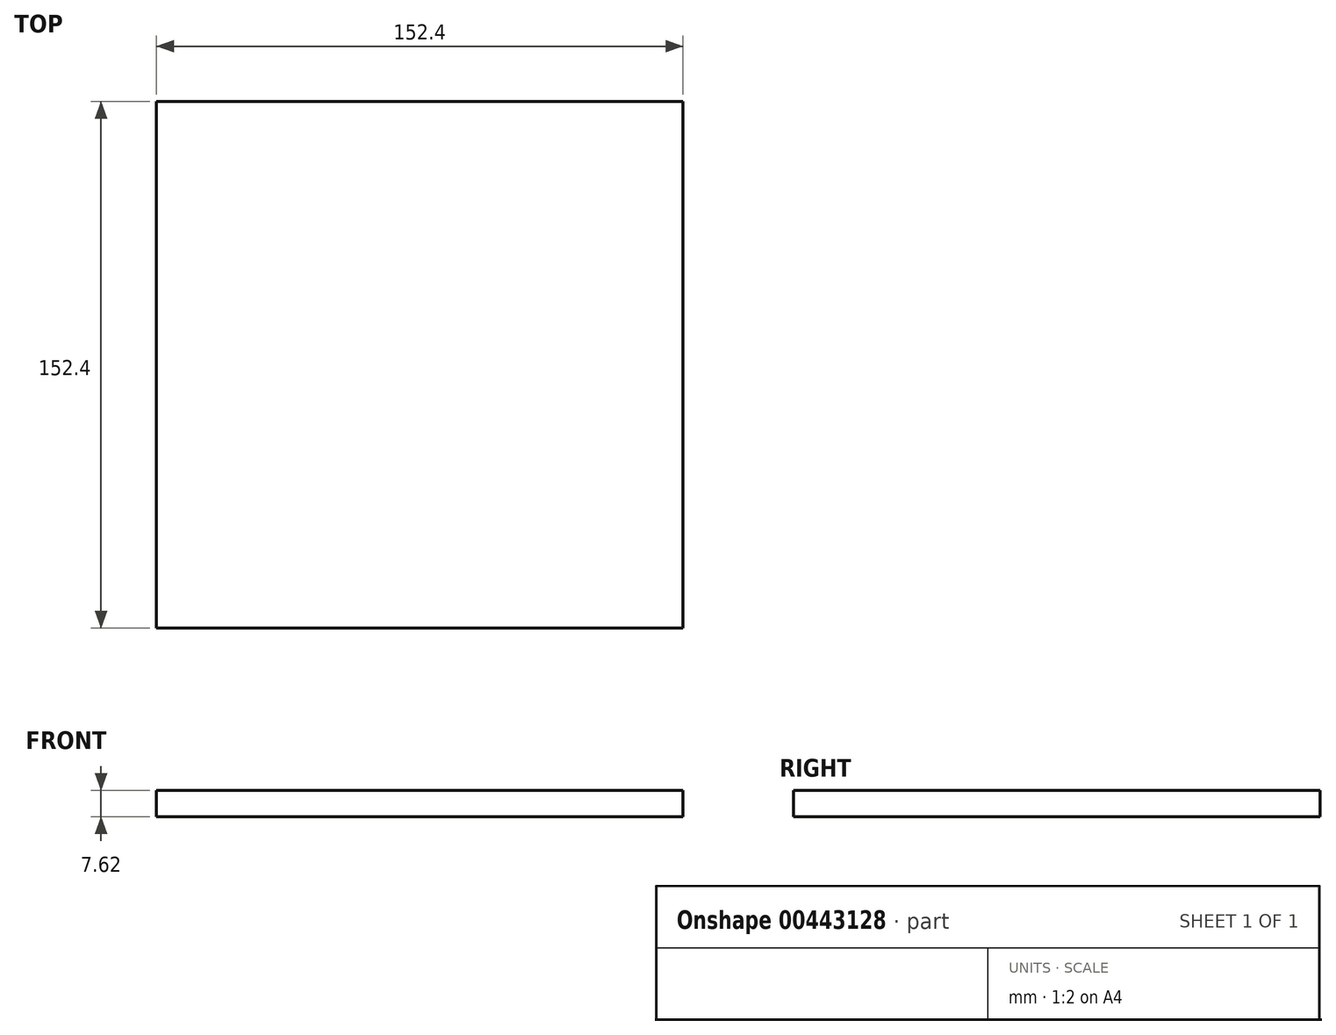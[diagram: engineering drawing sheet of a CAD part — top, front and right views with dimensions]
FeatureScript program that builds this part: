
annotation { "Feature Type Name" : "Feature", "Feature Type Description" : "" }
export const myFeature = defineFeature(function(context is Context, id is Id, definition is map)
    precondition{}
    {
        {
            var Q0;
            Q0=qCreatedBy(makeId("Top.planeOp"),FACE);
            var sketch = newSketch(context, id + "F0", { "sketchPlane" : qUnion([Q0])});
            skLineSegment(sketch, "E0", {"start": v(-60.57, 81.62) * mm, "end": v(91.83, 81.62) * mm});
            skLineSegment(sketch, "E1", {"start": v(91.83, 81.62) * mm, "end": v(91.83, -70.78) * mm});
            skLineSegment(sketch, "E2", {"start": v(91.83, -70.78) * mm, "end": v(-60.57, -70.78) * mm});
            skLineSegment(sketch, "E3", {"start": v(-60.57, -70.78) * mm, "end": v(-60.57, 81.62) * mm});
            skSolve(sketch);
        }
        {
            var Q0;
            Q0 = qSketchRegion(id + "F0", true);
            extrude(context, id + "F1", {"entities" : qUnion([Q0]), "depth" : 7.62 * mm});
        }
    });
